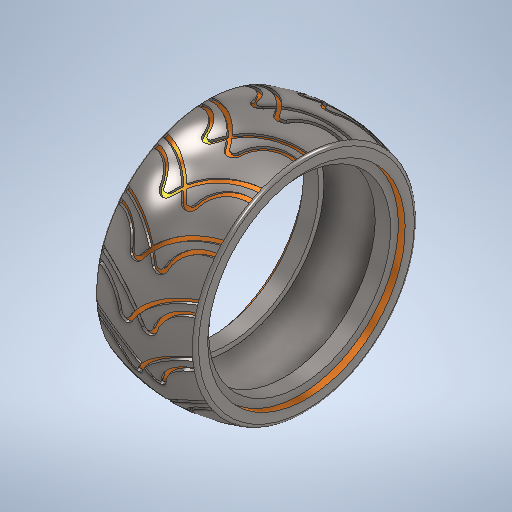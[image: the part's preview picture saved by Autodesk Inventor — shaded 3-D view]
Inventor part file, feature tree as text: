
AUTODESK INVENTOR PART (.ipt)
format: ipt  version: 2025 (Build 290162000, 162)  size: 1,521,152 bytes
history: native  units: in
note: dims shown in document units (in); Inventor stores cm internally (conversion verified against a paired STEP export)
features: sketch x3, revolve x2, plane x1, extrude x1, pattern_circular x1, mirror x1, other x1
ambient origin geometry x8: Origin, YZ Plane, XZ Plane, XY Plane, X Axis, Y Axis, Z Axis, Center Point
bodies: Solid1 (feature_tree)
feature tree (10):
  revolve  "Revolution1"  [1 undecoded]
  plane  "Work Plane1"
  extrude  "Extrusion1"  Depth=0.1598in
  pattern_circular  "Circular Pattern1"  [2 undecoded]
  mirror  "Mirror1"
  sketch  "Sketch1"  dims[d0=1.0449in d1=0.9425in]
  sketch  "Sketch2"  dims[d2=0.2925in d3=0.1598in]
  other  "Srf1"
  sketch  "Sketch3"  dims[d4=0.0799in d5=0.0701in d6=0.1232in d7=1.2354in d8=0.0394in d9=0.0394in d10=0.0522in d11=90.0deg d12=0.0276in d13=90.0deg d14=1.4469in d15=0.0394in d16=0.0394in d17=0.3937in d18=0.0in d19=5.9055in d20=360.0deg]
  revolve  "RevolutionSrf1"  [1 undecoded]
note: 4 required parameter values undecoded (feature->parameter linkage not recoverable at this tier; creation-order binding heuristic only, values carry confidence <= 0.55)